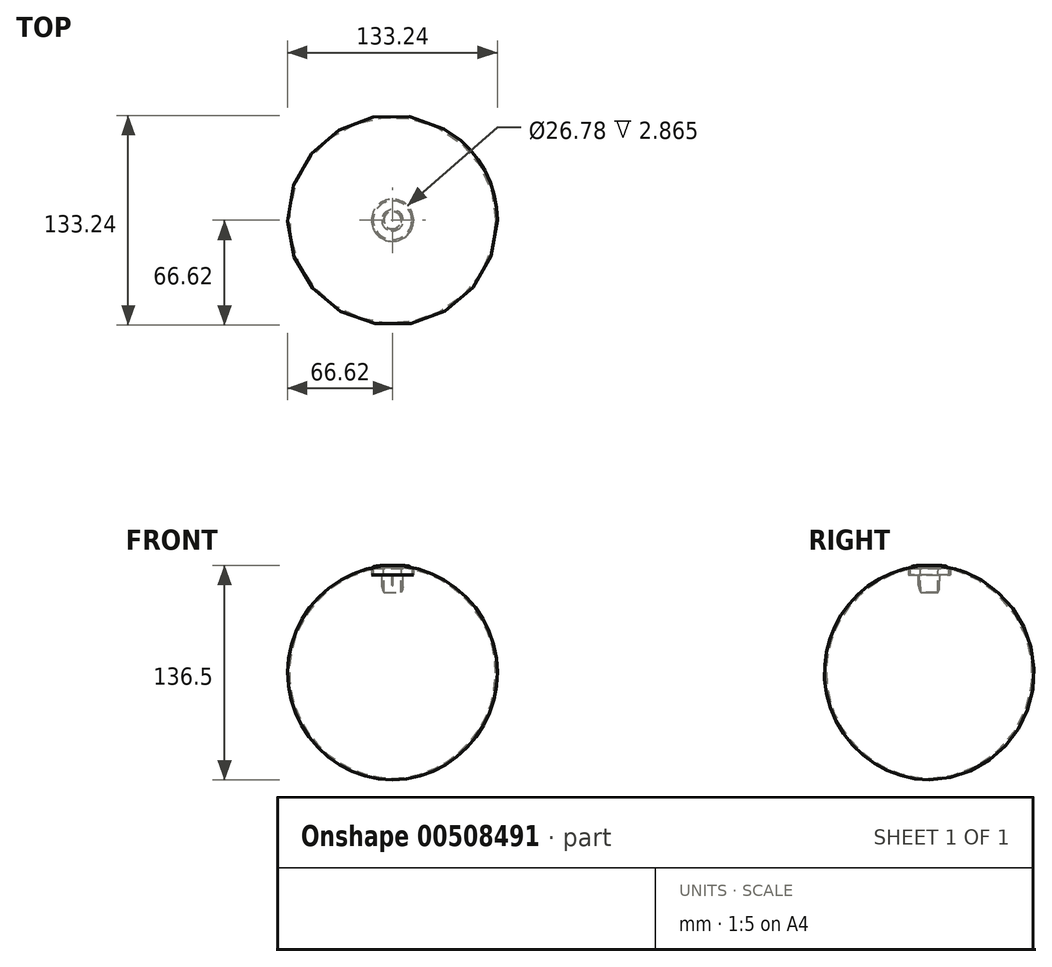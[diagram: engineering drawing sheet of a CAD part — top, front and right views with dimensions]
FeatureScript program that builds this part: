
annotation { "Feature Type Name" : "Feature", "Feature Type Description" : "" }
export const myFeature = defineFeature(function(context is Context, id is Id, definition is map)
    precondition{}
    {
        {
            var Q0;
            Q0=qCreatedBy(makeId("Front.planeOp"),FACE);
            var sketch = newSketch(context, id + "F0", { "sketchPlane" : qUnion([Q0])});
            skLineSegment(sketch, "E0.bottom", {"start": v(-13.39, 8.63) * mm, "end": v(13.4, 8.63) * mm, "construction": true});
            skLineSegment(sketch, "E0.top", {"start": v(-13.4, -8.63) * mm, "end": v(13.39, -8.63) * mm, "construction": true});
            skLineSegment(sketch, "E0.left", {"start": v(-13.39, 8.63) * mm, "end": v(-13.4, -8.63) * mm, "construction": true});
            skLineSegment(sketch, "E0.right", {"start": v(13.4, 8.63) * mm, "end": v(13.39, -8.63) * mm, "construction": true});
            skPoint(sketch, "E0.middle", {"position": v(0, 0) * mm});
            skPoint(sketch, "E1", {"position": v(0, 8.63) * mm});
            skArc(sketch, "E2", {"start": v(13.39, 7.63) * mm, "mid": v(6.72, 8.46) * mm, "end": v(0, 8.63) * mm});
            skLineSegment(sketch, "E3", {"start": v(13.39, 7.63) * mm, "end": v(13.4, 2.63) * mm});
            skArc(sketch, "E4.0", {"start": v(12.3, 6.7) * mm, "mid": v(9.55, 7.08) * mm, "end": v(6.8, 7.35) * mm});
            skLineSegment(sketch, "E5", {"start": v(0, 8.63) * mm, "end": v(0, 7.53) * mm});
            skLineSegment(sketch, "E6.0", {"start": v(12.3, 6.7) * mm, "end": v(12.3, 2.63) * mm});
            skLineSegment(sketch, "E7", {"start": v(12.3, 2.63) * mm, "end": v(13.4, 2.63) * mm});
            skLineSegment(sketch, "E8", {"start": v(0, 0) * mm, "end": v(0, 4.24) * mm, "construction": true});
            skLineSegment(sketch, "E9", {"start": v(5.38, -8.63) * mm, "end": v(6.48, -8.63) * mm});
            skLineSegment(sketch, "E10", {"start": v(6.48, -8.63) * mm, "end": v(6.8, 7.35) * mm});
            skLineSegment(sketch, "E11.0", {"start": v(5.38, -8.63) * mm, "end": v(5.7, 7.43) * mm});
            skPoint(sketch, "E12.orphan", {"position": v(0, -8.63) * mm});
            skArc(sketch, "E13.trimOffspring", {"start": v(5.7, 7.43) * mm, "mid": v(2.85, 7.54) * mm, "end": v(0, 7.53) * mm});
            skSolve(sketch);
        }
        {
            var Q0;
            Q0 = qSketchRegion(id + "F0", true);
            var Q1;
            Q1=sQuery(id+"F0.wireOp",EDGE,"E8");
            revolve(context, id + "F1", {"entities" : qUnion([Q0]), "axis" : qUnion([Q1]), "revolveType" : RevolveType.FULL});
        }
        {
            var Q0;
            Q0=makeQuery(id+"F1.opRevolve","SWEPT_EDGE",EDGE,{"disambiguationData":[OSD([sQuery(id+"F0.wireOp",EDGE,"E2"),sQuery(id+"F0.wireOp",EDGE,"E3")])]});
            fillet(context, id + "F2", {"entities" : qUnion([Q0]), "radius" : 2.5 * mm, "tangentPropagation" : true, "allowEdgeOverflow" : false});
        }
        {
            var Q0;
            Q0=makeQuery(id+"F1.opRevolve","SWEPT_EDGE",EDGE,{"disambiguationData":[OSD([sQuery(id+"F0.wireOp",EDGE,"E9"),sQuery(id+"F0.wireOp",EDGE,"E10")])]});
            fillet(context, id + "F3", {"entities" : qUnion([Q0]), "radius" : 6 * mm, "tangentPropagation" : true, "allowEdgeOverflow" : false});
        }
        {
            var Q0;
            Q0=qCreatedBy(makeId("Right.planeOp"),FACE);
            var sketch = newSketch(context, id + "F4", { "sketchPlane" : qUnion([Q0])});
            skLineSegment(sketch, "E14", {"start": v(-6.55, -5.2) * mm, "end": v(-6.57, -4.2) * mm});
            skLineSegment(sketch, "E15", {"start": v(-6.69, 1.63) * mm, "end": v(-7.19, 1.63) * mm});
            skLineSegment(sketch, "E16", {"start": v(-6.57, -4.2) * mm, "end": v(-7.07, -4.2) * mm});
            skLineSegment(sketch, "E17.0", {"start": v(13.4, 2.63) * mm, "end": v(-13.4, 2.63) * mm});
            skPoint(sketch, "E18", {"position": v(-6.7, 2.63) * mm});
            skLineSegment(sketch, "E19.0", {"start": v(-6.55, -5.2) * mm, "end": v(6.55, -5.2) * mm});
            skPoint(sketch, "E20", {"position": v(-6.55, -5.2) * mm});
            skLineSegment(sketch, "E21", {"start": v(-7.19, 1.63) * mm, "end": v(-7.07, -4.2) * mm});
            skLineSegment(sketch, "E22.0", {"start": v(-6.3, -5.19) * mm, "end": v(-6.55, 7.36) * mm});
            skLineSegment(sketch, "E23", {"start": v(-6.69, 1.63) * mm, "end": v(-6.44, 1.63) * mm});
            skLineSegment(sketch, "E24", {"start": v(-6.57, -4.2) * mm, "end": v(-6.32, -4.19) * mm});
            skLineSegment(sketch, "E25.trimOffspring", {"start": v(-6.69, 1.63) * mm, "end": v(-6.8, 7.35) * mm});
            skSolve(sketch);
        }
        {
            var Q0;
            {var subQ0=sQuery(id+"F4.wireOp",EDGE,"E15");Q0=makeQuery(id+"F4.imprint","IMPRINT",FACE,{"disambiguationData":[TD([[makeQuery(id+"F4.imprint","IMPRINT",EDGE,{"derivedFrom":subQ0}),1.0]])]});}
            extrude(context, id + "F5", {"entities" : qUnion([Q0]), "endBound" : BoundingType.SYMMETRIC, "depth" : .5 * mm});
        }
        {
            var Q0;
            Q0=makeQuery(id+"F5.opExtrude","CAP_EDGE",EDGE,{"disambiguationData":[OSD([sQuery(id+"F4.wireOp",EDGE,"E16")])],"isStart":true});
            var Q1;
            Q1=makeQuery(id+"F5.opExtrude","CAP_EDGE",EDGE,{"disambiguationData":[OSD([sQuery(id+"F4.wireOp",EDGE,"E16")])],"isStart":false});
            var Q2;
            Q2=makeQuery(id+"F5.opExtrude","CAP_EDGE",EDGE,{"disambiguationData":[OSD([sQuery(id+"F4.wireOp",EDGE,"E15"),sQuery(id+"F4.wireOp",EDGE,"E23")])],"isStart":true});
            var Q3;
            Q3=makeQuery(id+"F5.opExtrude","CAP_EDGE",EDGE,{"disambiguationData":[OSD([sQuery(id+"F4.wireOp",EDGE,"E15"),sQuery(id+"F4.wireOp",EDGE,"E23")])],"isStart":false});
            fillet(context, id + "F6", {"entities" : qUnion([Q0, Q1, Q2, Q3]), "radius" : .125 * mm, "tangentPropagation" : true, "allowEdgeOverflow" : false});
        }
        {
            var Q0;
            Q0=makeQuery(id+"F5.opExtrude","SWEPT_FACE",FACE,{"disambiguationData":[OSD([sQuery(id+"F4.wireOp",EDGE,"E21")])]});
            fillet(context, id + "F7", {"entities" : qUnion([Q0]), "radius" : .125 * mm, "tangentPropagation" : true, "allowEdgeOverflow" : false});
        }
    });
